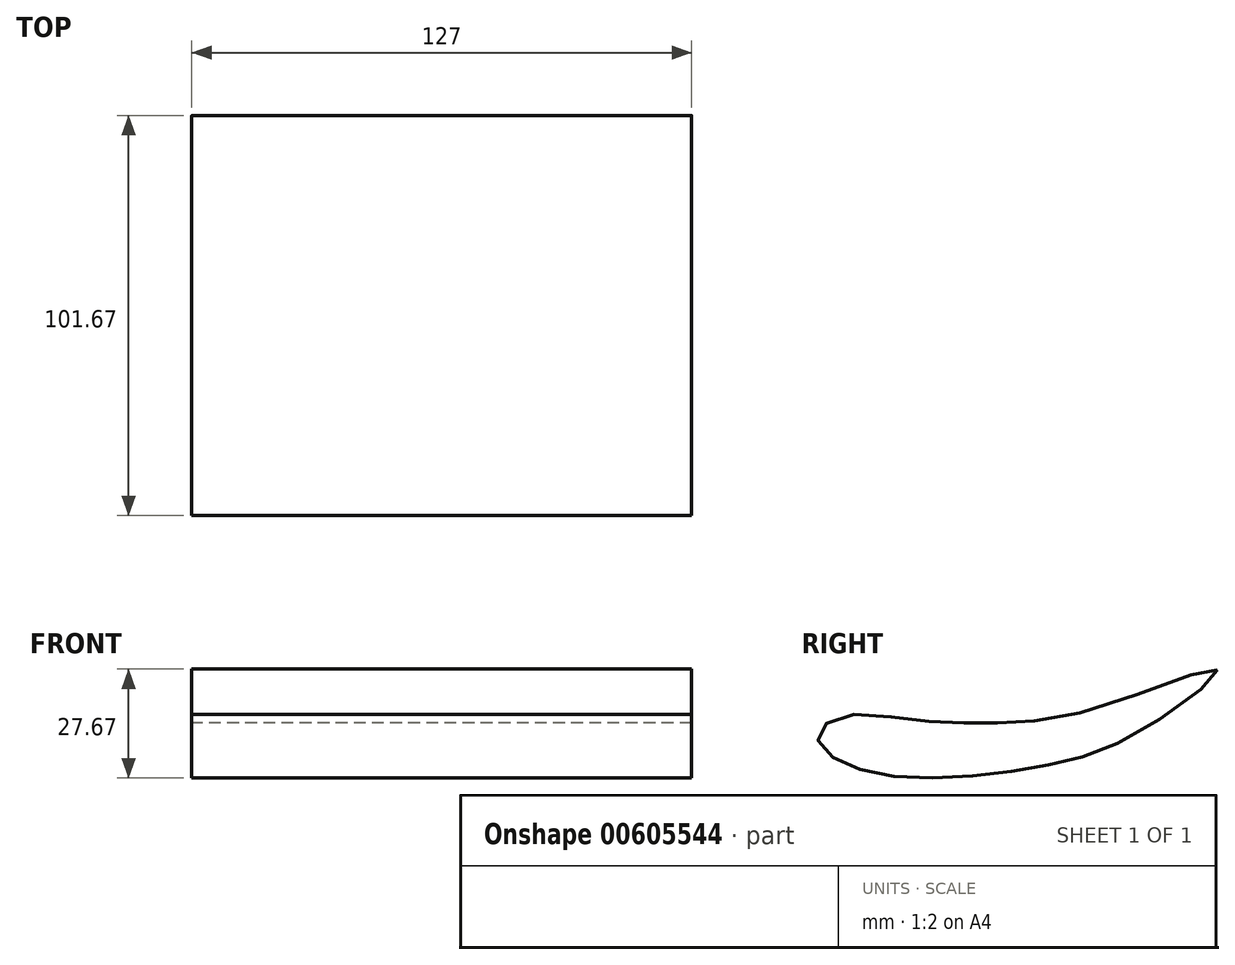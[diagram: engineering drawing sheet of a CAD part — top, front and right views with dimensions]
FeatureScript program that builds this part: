
annotation { "Feature Type Name" : "Feature", "Feature Type Description" : "" }
export const myFeature = defineFeature(function(context is Context, id is Id, definition is map)
    precondition{}
    {
        {
            var Q0;
            Q0=qCreatedBy(makeId("Right.planeOp"),FACE);
            var sketch = newSketch(context, id + "F0", { "sketchPlane" : qUnion([Q0])});
            skFitSpline(sketch, "E0", {"points": [v(38.36, 29.73) * mm, v(6.23, 19.69) * mm, v(-19.66, 16.34) * mm, v(-37.5, 17.01) * mm, v(-57.36, 17.9) * mm, v(-63.24, 12.95) * mm, v(-59.37, 7.64) * mm, v(-45.32, 2.95) * mm, v(-22.56, 2.95) * mm, v(-1.58, 6.3) * mm, v(19.4, 14.56) * mm, v(38.36, 29.73) * mm]});
            skSolve(sketch);
        }
        {
            var Q0;
            Q0 = qSketchRegion(id + "F0", true);
            extrude(context, id + "F1", {"entities" : qUnion([Q0]), "endBound" : BoundingType.SYMMETRIC, "depth" : 127 * mm, "offsetDistance" : 25.4 * mm});
        }
    });
